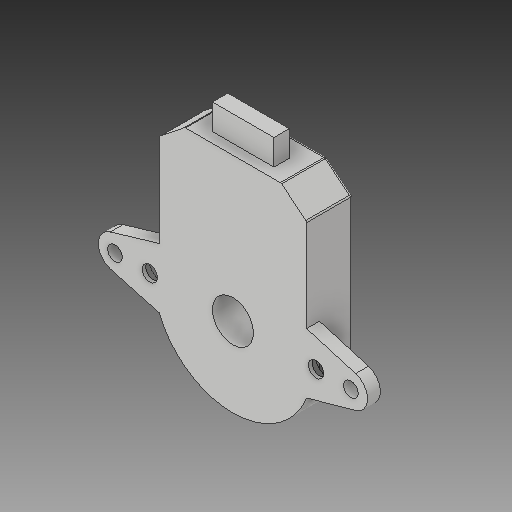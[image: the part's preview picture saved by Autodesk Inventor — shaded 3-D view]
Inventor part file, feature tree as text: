
AUTODESK INVENTOR PART (.ipt)
format: ipt  version: 2019 (Build 230136000, 136)  size: 223,744 bytes
history: native  units: mm
features: sketch x7, hole x4, extrude x3, fillet x2, other x1
ambient origin geometry x8: Origin, YZ Plane, XZ Plane, XY Plane, X Axis, Y Axis, Z Axis, Center Point
bodies: Body1 (feature_tree)
feature tree (17):
  other  "ソリッド1"
  extrude  "押し出し1"  Depth=28.77mm
  hole  "穴1"  [1 undecoded]
  extrude  "押し出し2"  Depth=4.0mm
  hole  "穴2"  [1 undecoded]
  hole  "穴3"  [1 undecoded]
  hole  "穴4"  [1 undecoded]
  fillet  "フィレット1"  Radius=9.0mm
  fillet  "フィレット2"  Radius=5.938155mm
  extrude  "押し出し3"  Depth=6.5mm
  sketch  "スケッチ1"
  sketch  "スケッチ2"
  sketch  "スケッチ3"
  sketch  "スケッチ4"
  sketch  "スケッチ5"
  sketch  "スケッチ6"
  sketch  "スケッチ7"
note: 4 required parameter values undecoded (feature->parameter linkage not recoverable at this tier; creation-order binding heuristic only, values carry confidence <= 0.55)
